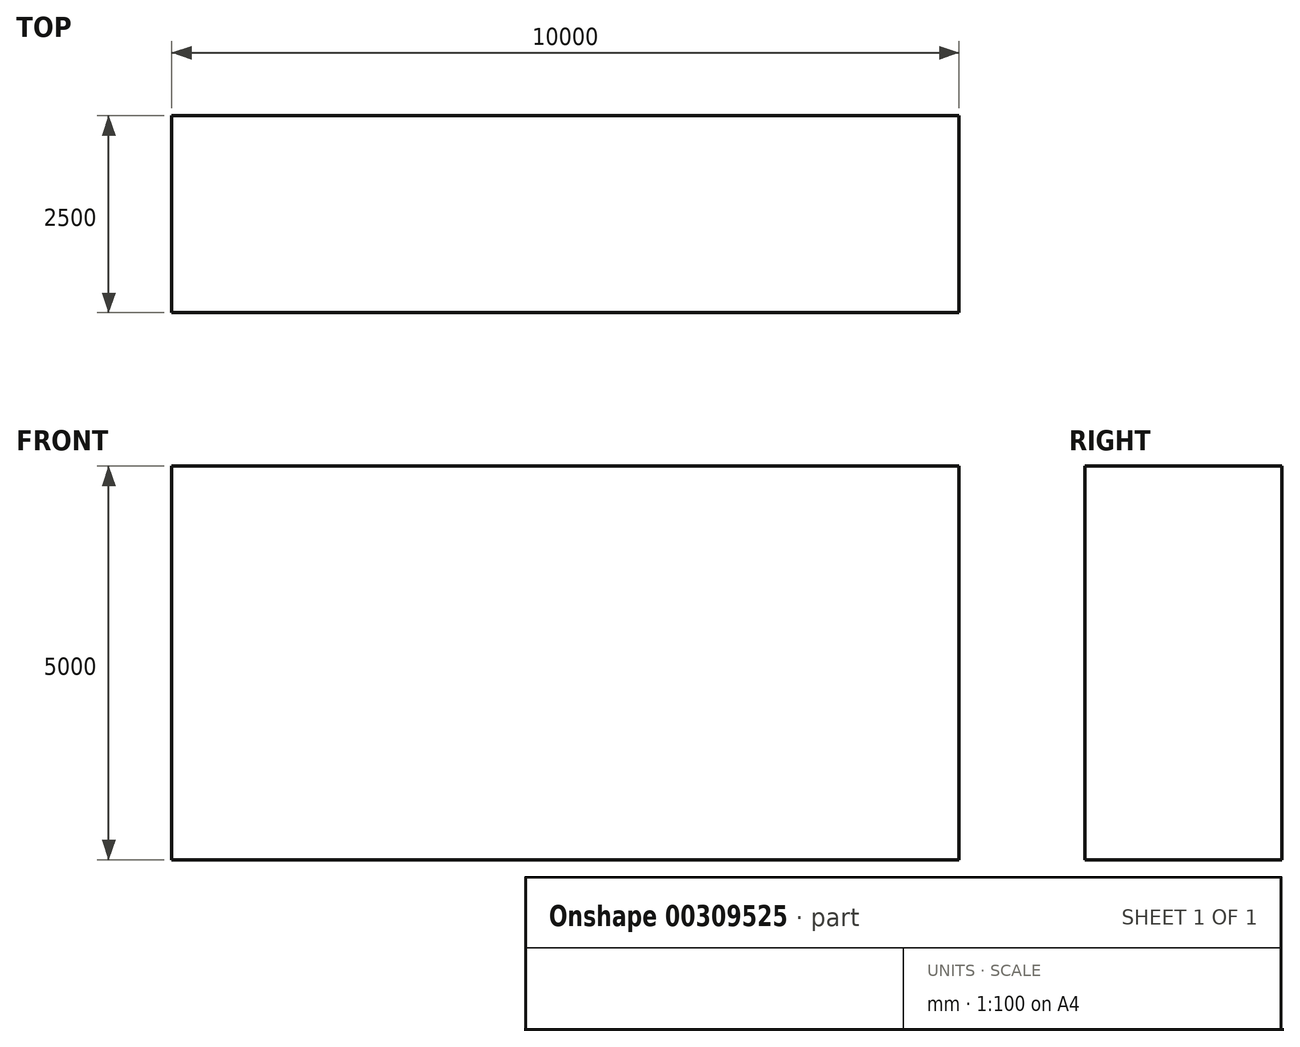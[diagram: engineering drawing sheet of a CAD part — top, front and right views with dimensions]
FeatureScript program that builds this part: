
annotation { "Feature Type Name" : "Feature", "Feature Type Description" : "" }
export const myFeature = defineFeature(function(context is Context, id is Id, definition is map)
    precondition{}
    {
        {
            var Q0;
            Q0=qCreatedBy(makeId("Front.planeOp"),FACE);
            var sketch = newSketch(context, id + "F0", { "sketchPlane" : qUnion([Q0])});
            skLineSegment(sketch, "E0.bottom", {"start": v(-4995.47, 2555.6) * mm, "end": v(5004.53, 2555.6) * mm});
            skLineSegment(sketch, "E0.top", {"start": v(-4995.47, -2444.4) * mm, "end": v(5004.53, -2444.4) * mm});
            skLineSegment(sketch, "E0.left", {"start": v(-4995.47, 2555.6) * mm, "end": v(-4995.47, -2444.4) * mm});
            skLineSegment(sketch, "E0.right", {"start": v(5004.53, 2555.6) * mm, "end": v(5004.53, -2444.4) * mm});
            skSolve(sketch);
        }
        {
            var Q0;
            Q0=makeQuery(id+"F0.imprint","IMPRINT",FACE,{"disambiguationData":[TD([[makeQuery(id+"F0.imprint","IMPRINT",EDGE,{"derivedFrom":sQuery(id+"F0.wireOp",EDGE,"E0.bottom")}),-1.0]])]});
            extrude(context, id + "F1", {"entities" : qUnion([Q0]), "depth" : 2500 * mm});
        }
    });
